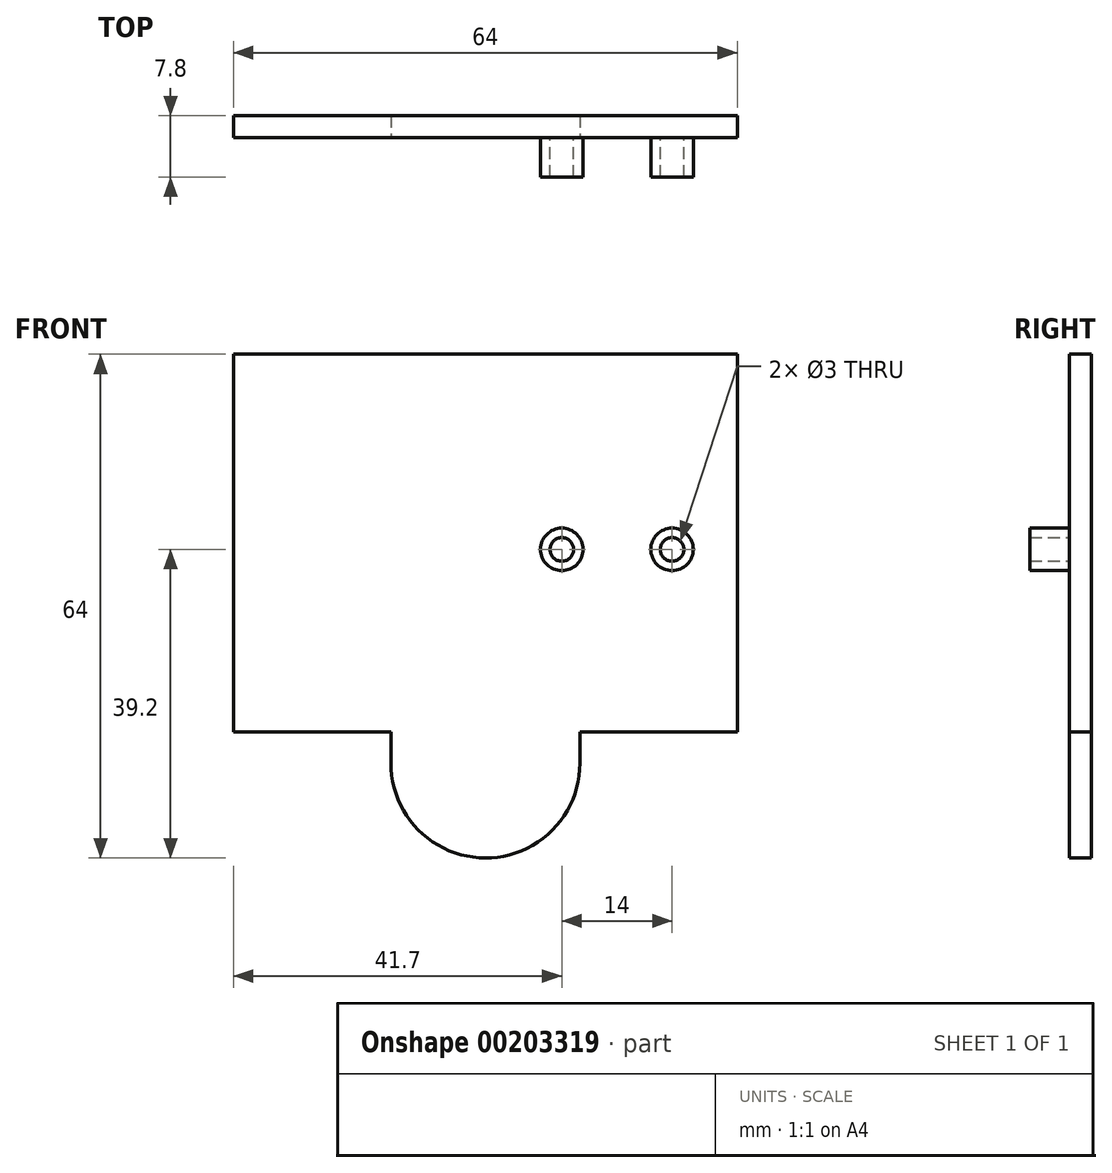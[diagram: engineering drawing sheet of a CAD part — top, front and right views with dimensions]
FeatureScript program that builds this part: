
annotation { "Feature Type Name" : "Feature", "Feature Type Description" : "" }
export const myFeature = defineFeature(function(context is Context, id is Id, definition is map)
    precondition{}
    {
        {
            var Q0;
            Q0=qCreatedBy(makeId("Front.planeOp"),FACE);
            var sketch = newSketch(context, id + "F0", { "sketchPlane" : qUnion([Q0])});
            skLineSegment(sketch, "E0.bottom", {"start": v(32, -24) * mm, "end": v(12, -24) * mm});
            skLineSegment(sketch, "E0.top", {"start": v(32, 24) * mm, "end": v(-32, 24) * mm});
            skLineSegment(sketch, "E0.left", {"start": v(32, -24) * mm, "end": v(32, 24) * mm});
            skLineSegment(sketch, "E0.right", {"start": v(-32, -24) * mm, "end": v(-32, 24) * mm});
            skPoint(sketch, "E0.middle", {"position": v(0, 0) * mm});
            skCircle(sketch, "E1", {"center": v(23.7, -0.8) * mm, "radius": 2.7 * mm});
            skCircle(sketch, "E2", {"center": v(9.7, -0.8) * mm, "radius": 2.7 * mm});
            skCircle(sketch, "E3", {"center": v(23.7, -0.8) * mm, "radius": 1.5 * mm});
            skCircle(sketch, "E4", {"center": v(9.7, -0.8) * mm, "radius": 1.5 * mm});
            skArc(sketch, "E5", {"start": v(-12, -27.9) * mm, "mid": v(-0.03, -40) * mm, "end": v(12, -27.96) * mm});
            skLineSegment(sketch, "E6", {"start": v(12, -28.04) * mm, "end": v(12, -24) * mm});
            skLineSegment(sketch, "E7", {"start": v(-12, -27.9) * mm, "end": v(-12, -24) * mm});
            skLineSegment(sketch, "E8.trimOffspring", {"start": v(-12, -24) * mm, "end": v(-32, -24) * mm});
            skSolve(sketch);
        }
        {
            var Q0;
            Q0=makeQuery(id+"F0.imprint","IMPRINT",FACE,{"disambiguationData":[TD([[makeQuery(id+"F0.imprint","IMPRINT",EDGE,{"derivedFrom":sQuery(id+"F0.wireOp",EDGE,"E1")}),1.0]])]});
            var Q1;
            Q1=makeQuery(id+"F0.imprint","IMPRINT",FACE,{"disambiguationData":[TD([[makeQuery(id+"F0.imprint","IMPRINT",EDGE,{"derivedFrom":sQuery(id+"F0.wireOp",EDGE,"E2")}),1.0]])]});
            extrude(context, id + "F1", {"entities" : qUnion([Q0, Q1]), "depth" : 5 * mm});
        }
        {
            var Q0;
            Q0 = qSketchRegion(id + "F0", true);
            var Q1;
            Q1=makeQuery(id+"F0.imprint","IMPRINT",FACE,{"disambiguationData":[TD([[makeQuery(id+"F0.imprint","IMPRINT",EDGE,{"derivedFrom":sQuery(id+"F0.wireOp",EDGE,"E2")}),1.0]])]});
            var Q2;
            Q2=makeQuery(id+"F0.imprint","IMPRINT",FACE,{"disambiguationData":[TD([[makeQuery(id+"F0.imprint","IMPRINT",EDGE,{"derivedFrom":sQuery(id+"F0.wireOp",EDGE,"E4")}),1.0]])]});
            var Q3;
            Q3=makeQuery(id+"F0.imprint","IMPRINT",FACE,{"disambiguationData":[TD([[makeQuery(id+"F0.imprint","IMPRINT",EDGE,{"derivedFrom":sQuery(id+"F0.wireOp",EDGE,"E1")}),1.0]])]});
            var Q4;
            Q4=makeQuery(id+"F0.imprint","IMPRINT",FACE,{"disambiguationData":[TD([[makeQuery(id+"F0.imprint","IMPRINT",EDGE,{"derivedFrom":sQuery(id+"F0.wireOp",EDGE,"E3")}),1.0]])]});
            extrude(context, id + "F2", {"entities" : qUnion([Q0, Q1, Q2, Q3, Q4]), "oppositeDirection" : true, "depth" : 2.8 * mm});
        }
    });
